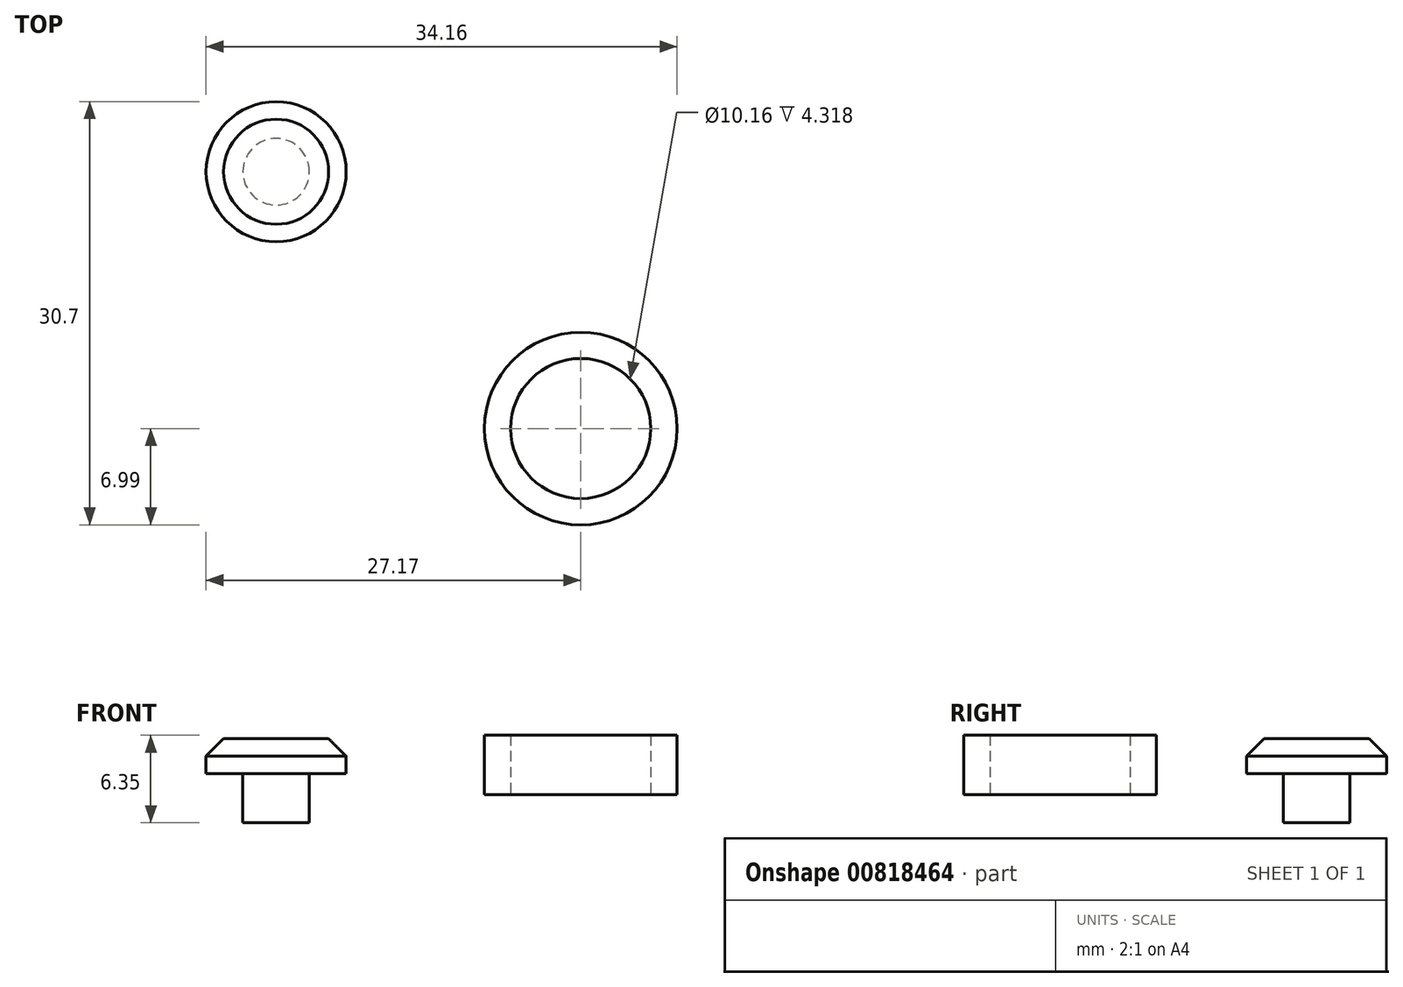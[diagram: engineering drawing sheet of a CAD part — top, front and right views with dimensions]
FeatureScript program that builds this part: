
annotation { "Feature Type Name" : "Feature", "Feature Type Description" : "" }
export const myFeature = defineFeature(function(context is Context, id is Id, definition is map)
    precondition{}
    {
        {
            var Q0;
            Q0=qCreatedBy(makeId("Top.planeOp"),FACE);
            var sketch = newSketch(context, id + "F0", { "sketchPlane" : qUnion([Q0])});
            skCircle(sketch, "E0", {"center": v(0, 0) * mm, "radius": 5.08 * mm});
            skCircle(sketch, "E1", {"center": v(0, 0) * mm, "radius": 6.99 * mm});
            skSolve(sketch);
        }
        {
            var Q0;
            Q0=makeQuery(id+"F0.imprint","IMPRINT",FACE,{"disambiguationData":[TD([[makeQuery(id+"F0.imprint","IMPRINT",EDGE,{"derivedFrom":sQuery(id+"F0.wireOp",EDGE,"E0")}),-1.0]])]});
            extrude(context, id + "F1", {"entities" : qUnion([Q0]), "depth" : 4.32 * mm, "offsetDistance" : 25.4 * mm});
        }
        {
            var Q0;
            Q0=qCreatedBy(makeId("Top.planeOp"),FACE);
            var sketch = newSketch(context, id + "F2", { "sketchPlane" : qUnion([Q0])});
            skCircle(sketch, "E2", {"center": v(-22.1, 18.63) * mm, "radius": 2.41 * mm});
            skSolve(sketch);
        }
        {
            var Q0;
            Q0=makeQuery(id+"F2.imprint","IMPRINT",FACE,{"disambiguationData":[TD([[makeQuery(id+"F2.imprint","IMPRINT",EDGE,{"derivedFrom":sQuery(id+"F2.wireOp",EDGE,"E2")}),1.0]])]});
            extrude(context, id + "F3", {"entities" : qUnion([Q0]), "depth" : 1.52 * mm, "offsetDistance" : 25.4 * mm});
        }
        {
            var Q0;
            Q0=makeQuery(id+"F3.opExtrude","CAP_FACE",FACE,{"disambiguationData":[OSD([sQuery(id+"F2.wireOp",EDGE,"E2")])],"isStart":false});
            var sketch = newSketch(context, id + "F4", { "sketchPlane" : qUnion([Q0])});
            skCircle(sketch, "E3", {"center": v(-22.1, 18.63) * mm, "radius": 5.08 * mm});
            skSolve(sketch);
        }
        {
            var Q0;
            Q0=makeQuery(id+"F4.imprint","IMPRINT",FACE,{"disambiguationData":[TD([[makeQuery(id+"F4.imprint","IMPRINT",EDGE,{"derivedFrom":makeQuery(id+"F3.opExtrude","CAP_EDGE",EDGE,{"disambiguationData":[OSD([sQuery(id+"F2.wireOp",EDGE,"E2")])],"isStart":false})}),1.0]])]});
            var Q1;
            Q1=makeQuery(id+"F4.imprint","IMPRINT",FACE,{"disambiguationData":[TD([[makeQuery(id+"F4.imprint","IMPRINT",EDGE,{"derivedFrom":sQuery(id+"F4.wireOp",EDGE,"E3")}),1.0]])]});
            extrude(context, id + "F5", {"entities" : qUnion([Q0, Q1]), "operationType" : NewBodyOperationType.ADD, "depth" : 2.54 * mm, "offsetDistance" : 25.4 * mm});
        }
        {
            var Q0;
            Q0=makeQuery(id+"F5.opExtrude","CAP_FACE",FACE,{"disambiguationData":[OSD([sQuery(id+"F4.wireOp",EDGE,"E3")])],"isStart":false});
            chamfer(context, id + "F6", {"entities" : qUnion([Q0]), "width" : 1.27 * mm, "tangentPropagation" : true});
        }
        {
            var Q0;
            Q0=makeQuery(id+"F3.opExtrude","CAP_FACE",FACE,{"disambiguationData":[OSD([sQuery(id+"F2.wireOp",EDGE,"E2")])],"isStart":true});
            extrude(context, id + "F7", {"entities" : qUnion([Q0]), "operationType" : NewBodyOperationType.ADD, "depth" : 2.03 * mm, "offsetDistance" : 25.4 * mm});
        }
    });
